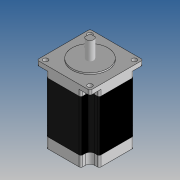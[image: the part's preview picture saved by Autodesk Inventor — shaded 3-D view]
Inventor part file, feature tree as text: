
AUTODESK INVENTOR PART (.ipt)
format: ipt  version: 2017 (Build 210142000, 142)  size: 268,800 bytes
history: native  units: mm
features: other x6, sketch x5, extrude x4, plane x2, split x2, fillet x1, revolve x1
ambient origin geometry x8: Origin, YZ Plane, XZ Plane, XY Plane, X Axis, Y Axis, Z Axis, Center Point
bodies: Body1 (feature_tree), Body2 (feature_tree), Body3 (feature_tree), Body4 (feature_tree)
feature tree (21):
  other  "Sólido1"
  extrude  "Extrusión1"  Depth=2.0mm
  extrude  "Extrusión2"  Depth=61.609459mm
  extrude  "Extrusión3"  Depth=4.7mm TaperAngle=0.0deg
  fillet  "Empalme1"  Radius=37.0mm
  plane  "Plano de trabajo1"
  plane  "Plano de trabajo2"
  split  "Dividir1"
  split  "Dividir2"
  revolve  "Revolución1"  [1 undecoded]
  extrude  "Extrusión4"  [1 undecoded]
  sketch  "Boceto1"  dims[d0=56.4mm d1=2.0mm]
  sketch  "Boceto2"  dims[d2=5.0mm d3=61.609459mm]
  sketch  "Boceto3"  dims[d4=6.35mm d5=4.7mm d6=0.0mm d7=37.0mm]
  sketch  "Boceto4"  dims[d8=71.3mm d9=0.0mm d10=38.0mm]
  other  "Sólido6"
  sketch  "Boceto5"  dims[d11=1.6mm d12=0.0mm d13=-11.0mm d14=-11.0mm d15=2.0mm d16=8.0mm d17=19.0mm d18=90.0deg d19=7.4mm d20=2.0mm d21=10.0mm d22=0.0mm d23=47.1mm]
  other  "Sólido2"
  other  "Sólido3"
  other  "Sólido4"
  other  "Sólido5"
note: 2 required parameter values undecoded (feature->parameter linkage not recoverable at this tier; creation-order binding heuristic only, values carry confidence <= 0.55)